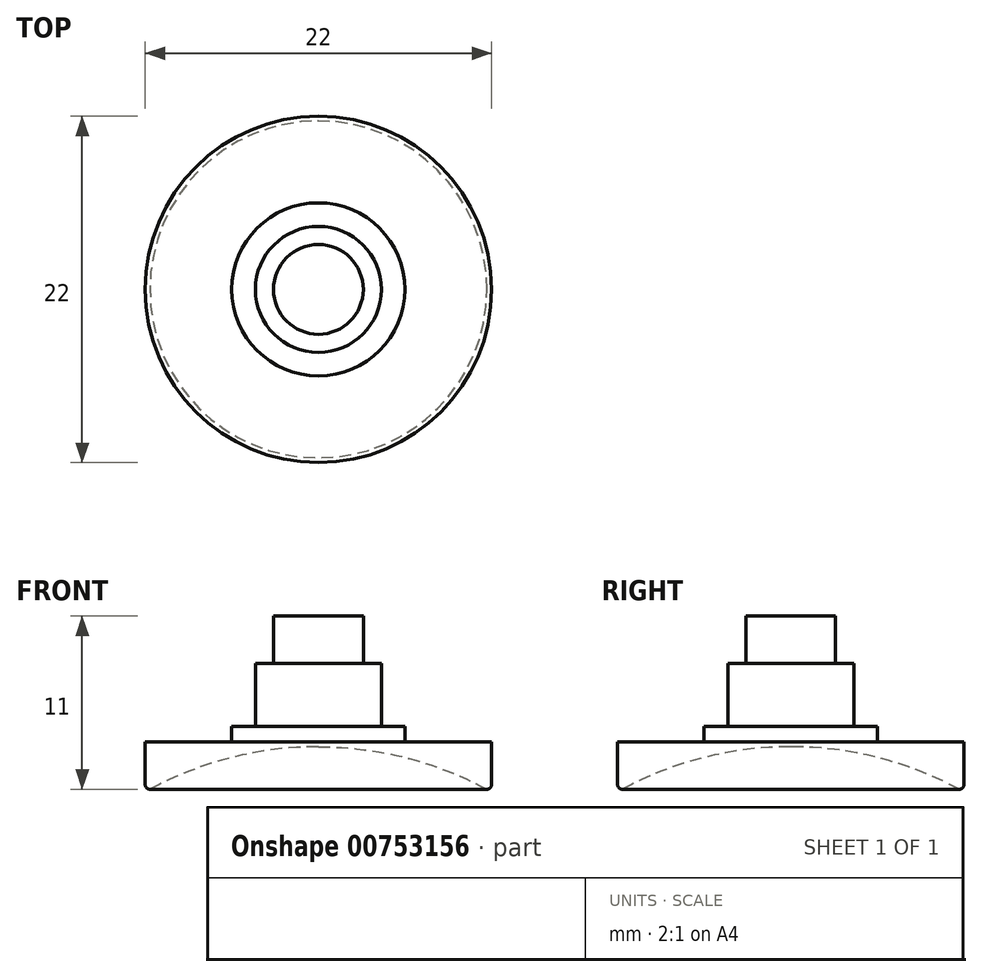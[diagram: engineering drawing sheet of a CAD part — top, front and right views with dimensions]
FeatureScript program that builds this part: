
annotation { "Feature Type Name" : "Feature", "Feature Type Description" : "" }
export const myFeature = defineFeature(function(context is Context, id is Id, definition is map)
    precondition{}
    {
        {
            var Q0;
            Q0=qCreatedBy(makeId("Top.planeOp"),FACE);
            var sketch = newSketch(context, id + "F0", { "sketchPlane" : qUnion([Q0])});
            skCircle(sketch, "E0", {"center": v(0, 0) * mm, "radius": 11 * mm});
            skSolve(sketch);
        }
        {
            var Q0;
            Q0=qSketchRegion(id+"F0",true);
            extrude(context, id + "F1", {"entities" : qUnion([Q0]), "depth" : 3 * mm, "offsetDistance" : 25 * mm});
        }
        {
            var Q0;
            Q0=qCreatedBy(makeId("Front.planeOp"),FACE);
            var sketch = newSketch(context, id + "F2", { "sketchPlane" : qUnion([Q0])});
            skLineSegment(sketch, "E1", {"start": v(0, 0) * mm, "end": v(0, -4.5) * mm, "construction": true});
            skSolve(sketch);
        }
        {
            var Q0;
            Q0=qCreatedBy(makeId("Front.planeOp"),FACE);
            var sketch = newSketch(context, id + "F3", { "sketchPlane" : qUnion([Q0])});
            skArc(sketch, "E2", {"start": v(0, 2.7) * mm, "mid": v(-22.55, -19.85) * mm, "end": v(0, -42.4) * mm});
            skLineSegment(sketch, "E3", {"start": v(0, 2.7) * mm, "end": v(0, -42.4) * mm});
            skPoint(sketch, "E4", {"position": v(-10.7, 0) * mm});
            skSolve(sketch);
        }
        {
            var Q0;
            Q0=qSketchRegion(id+"F3",true);
            var Q1;
            Q1=sQuery(id+"F3.wireOp",EDGE,"E3");
            revolve(context, id + "F4", {"operationType" : NewBodyOperationType.REMOVE, "surfaceOperationType" : NewSurfaceOperationType.NEW, "entities" : qUnion([Q0]), "axis" : qUnion([Q1]), "revolveType" : RevolveType.FULL, "oppositeDirection" : true});
        }
        {
            var Q0;
            Q0=makeQuery(id+"F1.opExtrude","CAP_FACE",FACE,{"disambiguationData":[OSD([sQuery(id+"F0.wireOp",EDGE,"E0")])],"isStart":false});
            var sketch = newSketch(context, id + "F5", { "sketchPlane" : qUnion([Q0])});
            skCircle(sketch, "E5", {"center": v(0, 0) * mm, "radius": 5.5 * mm});
            skSolve(sketch);
        }
        {
            var Q0;
            Q0=qSketchRegion(id+"F5",true);
            extrude(context, id + "F6", {"entities" : qUnion([Q0]), "operationType" : NewBodyOperationType.ADD, "depth" : 1 * mm, "offsetDistance" : 25 * mm});
        }
        {
            var Q0;
            Q0=makeQuery(id+"F6.opExtrude","CAP_FACE",FACE,{"disambiguationData":[OSD([sQuery(id+"F5.wireOp",EDGE,"E5")])],"isStart":false});
            var sketch = newSketch(context, id + "F7", { "sketchPlane" : qUnion([Q0])});
            skCircle(sketch, "E6", {"center": v(0, 0) * mm, "radius": 4 * mm});
            skSolve(sketch);
        }
        {
            var Q0;
            Q0=qSketchRegion(id+"F7",true);
            extrude(context, id + "F8", {"entities" : qUnion([Q0]), "operationType" : NewBodyOperationType.ADD, "depth" : 4 * mm, "offsetDistance" : 25 * mm});
        }
        {
            var Q0;
            Q0=makeQuery(id+"F8.opExtrude","CAP_FACE",FACE,{"disambiguationData":[OSD([sQuery(id+"F7.wireOp",EDGE,"E6")])],"isStart":false});
            var sketch = newSketch(context, id + "F9", { "sketchPlane" : qUnion([Q0])});
            skCircle(sketch, "E7", {"center": v(0, 0) * mm, "radius": 2.85 * mm});
            skSolve(sketch);
        }
        {
            var Q0;
            Q0=qSketchRegion(id+"F9",true);
            extrude(context, id + "F10", {"entities" : qUnion([Q0]), "operationType" : NewBodyOperationType.ADD, "depth" : 3 * mm, "offsetDistance" : 25 * mm});
        }
        {
            var Q0;
            Q0=makeQuery(id+"F1.opExtrude","CAP_EDGE",EDGE,{"disambiguationData":[OSD([sQuery(id+"F0.wireOp",EDGE,"E0")])],"isStart":true});
            fillet(context, id + "F11", {"entities" : qUnion([Q0]), "radius" : 0.3 * mm, "tangentPropagation" : true, "allowEdgeOverflow" : false});
        }
    });
